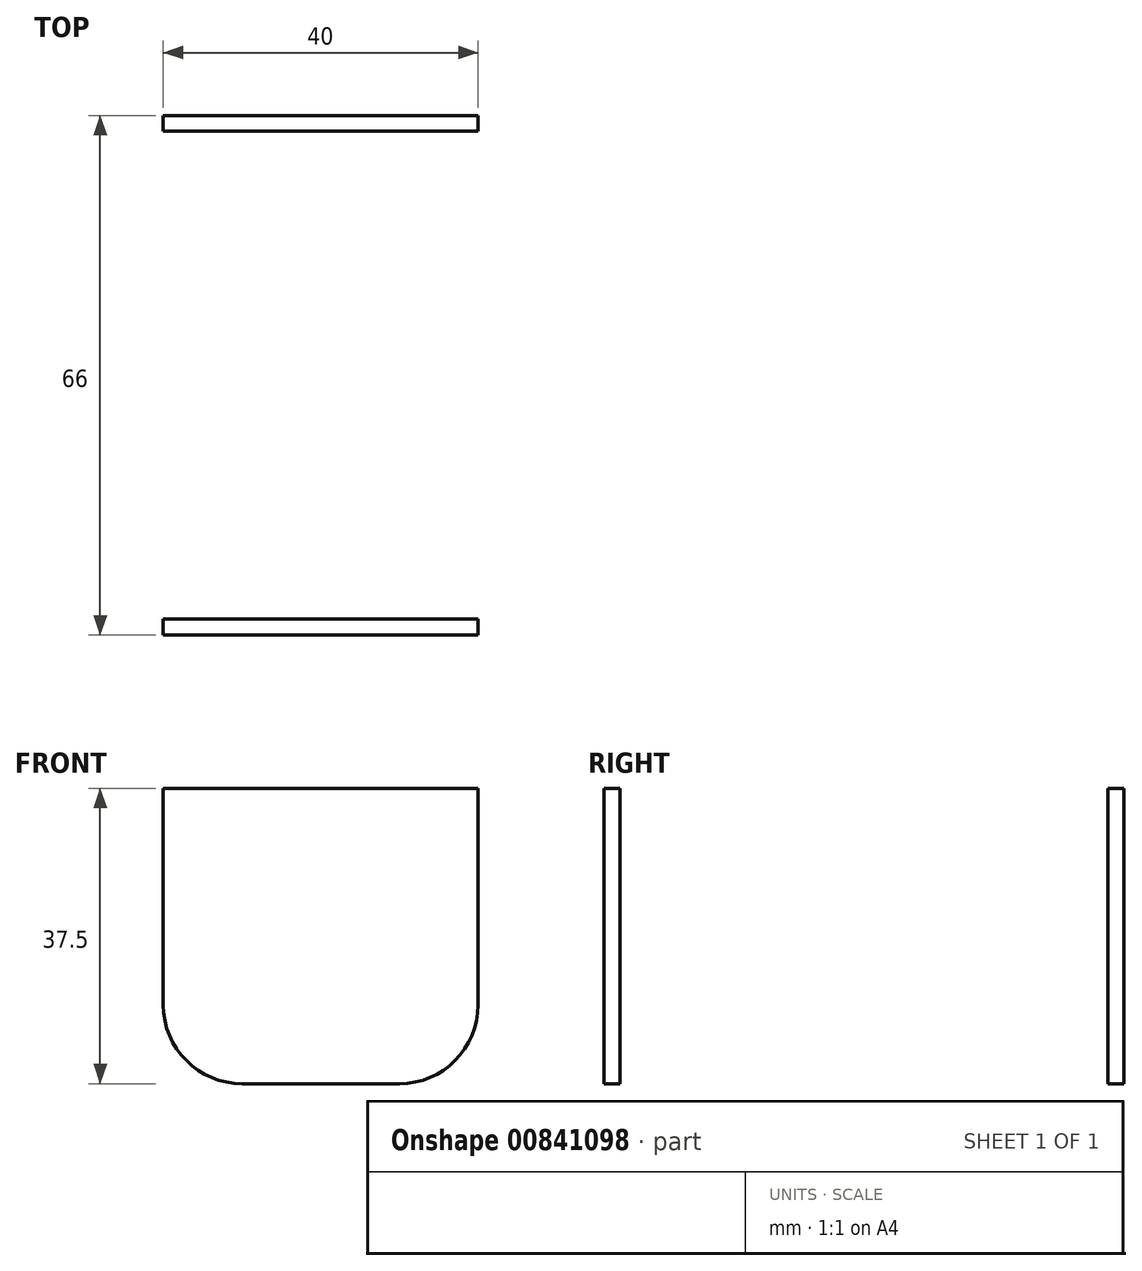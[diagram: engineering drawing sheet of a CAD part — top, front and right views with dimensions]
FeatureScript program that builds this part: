
annotation { "Feature Type Name" : "Feature", "Feature Type Description" : "" }
export const myFeature = defineFeature(function(context is Context, id is Id, definition is map)
    precondition{}
    {
        {
            var Q0;
            Q0=qCreatedBy(makeId("Top.planeOp"),FACE);
            var sketch = newSketch(context, id + "F0", { "sketchPlane" : qUnion([Q0])});
            skLineSegment(sketch, "E0.bottom", {"start": v(24.8, -33) * mm, "end": v(-24.8, -33) * mm});
            skLineSegment(sketch, "E0.top", {"start": v(24.8, 33) * mm, "end": v(-24.8, 33) * mm});
            skLineSegment(sketch, "E0.left", {"start": v(33, -24.8) * mm, "end": v(33, 24.8) * mm});
            skLineSegment(sketch, "E0.right", {"start": v(-33, -24.8) * mm, "end": v(-33, 24.8) * mm});
            skPoint(sketch, "E0.middle", {"position": v(0, 0) * mm});
            skPoint(sketch, "E1.visualSharp", {"position": v(-33, 33) * mm});
            skArc(sketch, "E1.filletArc", {"start": v(-24.8, 33) * mm, "mid": v(-30.6, 30.6) * mm, "end": v(-33, 24.8) * mm});
            skPoint(sketch, "E2.visualSharp", {"position": v(33, 33) * mm});
            skArc(sketch, "E2.filletArc", {"start": v(33, 24.8) * mm, "mid": v(30.6, 30.6) * mm, "end": v(24.8, 33) * mm});
            skPoint(sketch, "E3.visualSharp", {"position": v(33, -33) * mm});
            skArc(sketch, "E3.filletArc", {"start": v(24.8, -33) * mm, "mid": v(30.6, -30.6) * mm, "end": v(33, -24.8) * mm});
            skPoint(sketch, "E4.visualSharp", {"position": v(-33, -33) * mm});
            skArc(sketch, "E4.filletArc", {"start": v(-33, -24.8) * mm, "mid": v(-30.6, -30.6) * mm, "end": v(-24.8, -33) * mm});
            skSolve(sketch);
        }
        {
            var Q0;
            Q0=qSketchRegion(id+"F0",true);
            extrude(context, id + "F1", {"entities" : qUnion([Q0]), "oppositeDirection" : true, "depth" : 50 * mm, "offsetDistance" : 25 * mm});
        }
        {
            var Q0;
            Q0=makeQuery(id+"F1.opExtrude","CAP_EDGE",EDGE,{"disambiguationData":[OSD([sQuery(id+"F0.wireOp",EDGE,"E0.bottom")])],"isStart":false});
            fillet(context, id + "F2", {"entities" : qUnion([Q0]), "radius" : 5 * mm, "tangentPropagation" : true, "allowEdgeOverflow" : false});
        }
        {
            var Q0;
            Q0=makeQuery(id+"F1.opExtrude","CAP_FACE",FACE,{"disambiguationData":[OSD([sQuery(id+"F0.wireOp",EDGE,"E0.bottom"),sQuery(id+"F0.wireOp",EDGE,"E0.top"),sQuery(id+"F0.wireOp",EDGE,"E0.left"),sQuery(id+"F0.wireOp",EDGE,"E0.right"),sQuery(id+"F0.wireOp",EDGE,"E1.filletArc"),sQuery(id+"F0.wireOp",EDGE,"E2.filletArc"),sQuery(id+"F0.wireOp",EDGE,"E3.filletArc"),sQuery(id+"F0.wireOp",EDGE,"E4.filletArc")])],"isStart":false});
            var sketch = newSketch(context, id + "F3", { "sketchPlane" : qUnion([Q0])});
            skLineSegment(sketch, "E5.bottom", {"start": v(24.8, -28) * mm, "end": v(-24.8, -28) * mm});
            skLineSegment(sketch, "E5.top", {"start": v(24.8, 28) * mm, "end": v(-24.8, 28) * mm});
            skLineSegment(sketch, "E5.left", {"start": v(28, -24.8) * mm, "end": v(28, 24.8) * mm});
            skLineSegment(sketch, "E5.right", {"start": v(-28, -24.8) * mm, "end": v(-28, 24.8) * mm});
            skPoint(sketch, "E5.middle", {"position": v(0, 0) * mm});
            skPoint(sketch, "E6.visualSharp", {"position": v(28, 28) * mm});
            skArc(sketch, "E6.filletArc", {"start": v(28, 24.8) * mm, "mid": v(27.06, 27.06) * mm, "end": v(24.8, 28) * mm});
            skPoint(sketch, "E7.visualSharp", {"position": v(28, -28) * mm});
            skArc(sketch, "E7.filletArc", {"start": v(24.8, -28) * mm, "mid": v(27.06, -27.06) * mm, "end": v(28, -24.8) * mm});
            skPoint(sketch, "E8.visualSharp", {"position": v(-28, -28) * mm});
            skArc(sketch, "E8.filletArc", {"start": v(-28, -24.8) * mm, "mid": v(-27.06, -27.06) * mm, "end": v(-24.8, -28) * mm});
            skPoint(sketch, "E9.visualSharp", {"position": v(-28, 28) * mm});
            skArc(sketch, "E9.filletArc", {"start": v(-24.8, 28) * mm, "mid": v(-27.06, 27.06) * mm, "end": v(-28, 24.8) * mm});
            skArc(sketch, "E10.0", {"start": v(27, 24.8) * mm, "mid": v(26.36, 26.36) * mm, "end": v(24.8, 27) * mm});
            skLineSegment(sketch, "E10.1", {"start": v(27, -24.8) * mm, "end": v(27, 24.8) * mm});
            skLineSegment(sketch, "E10.2", {"start": v(24.8, 27) * mm, "end": v(-24.8, 27) * mm});
            skArc(sketch, "E10.3", {"start": v(24.8, -27) * mm, "mid": v(26.36, -26.36) * mm, "end": v(27, -24.8) * mm});
            skArc(sketch, "E10.4", {"start": v(-24.8, 27) * mm, "mid": v(-26.36, 26.36) * mm, "end": v(-27, 24.8) * mm});
            skLineSegment(sketch, "E10.5", {"start": v(-27, -24.8) * mm, "end": v(-27, 24.8) * mm});
            skArc(sketch, "E10.6", {"start": v(-27, -24.8) * mm, "mid": v(-26.36, -26.36) * mm, "end": v(-24.8, -27) * mm});
            skLineSegment(sketch, "E10.7", {"start": v(24.8, -27) * mm, "end": v(-24.8, -27) * mm});
            skSolve(sketch);
        }
        {
            var Q0;
            Q0=qSketchRegion(id+"F3",true);
            extrude(context, id + "F4", {"entities" : qUnion([Q0]), "operationType" : NewBodyOperationType.ADD, "depth" : 1 * mm, "offsetDistance" : 25 * mm});
        }
        {
            var Q0;
            Q0=makeQuery(id+"F1.opExtrude","CAP_FACE",FACE,{"disambiguationData":[OSD([sQuery(id+"F0.wireOp",EDGE,"E0.bottom"),sQuery(id+"F0.wireOp",EDGE,"E0.top"),sQuery(id+"F0.wireOp",EDGE,"E0.left"),sQuery(id+"F0.wireOp",EDGE,"E0.right"),sQuery(id+"F0.wireOp",EDGE,"E1.filletArc"),sQuery(id+"F0.wireOp",EDGE,"E2.filletArc"),sQuery(id+"F0.wireOp",EDGE,"E3.filletArc"),sQuery(id+"F0.wireOp",EDGE,"E4.filletArc")])],"isStart":true});
            shell(context, id + "F5", {"entities" : qUnion([Q0]), "thickness" : 2 * mm});
        }
        {
            var Q0;
            Q0=qCreatedBy(makeId("Top.planeOp"),FACE);
            cPlane(context, id + "F6", {"entities" : qUnion([Q0]), "cplaneType" : CPlaneType.OFFSET, "offset" : 3 * mm, "oppositeDirection" : true, "width" : 150 * mm, "height" : 150 * mm});
        }
        {
            var Q0;
            Q0=qCreatedBy(id+"F6.planeOp",FACE);
            var sketch = newSketch(context, id + "F7", { "sketchPlane" : qUnion([Q0])});
            skArc(sketch, "E11", {"start": v(24.8, -33) * mm, "mid": v(30.6, -30.6) * mm, "end": v(33, -24.8) * mm});
            skArc(sketch, "E12.0", {"start": v(24.8, -32) * mm, "mid": v(29.9, -29.9) * mm, "end": v(32, -24.8) * mm});
            skLineSegment(sketch, "E13", {"start": v(32, -24.8) * mm, "end": v(33, -24.8) * mm});
            skLineSegment(sketch, "E14", {"start": v(24.8, -32) * mm, "end": v(24.8, -33) * mm});
            skSolve(sketch);
        }
        {
            var Q0;
            Q0=qSketchRegion(id+"F7",true);
            extrude(context, id + "F8", {"entities" : qUnion([Q0]), "operationType" : NewBodyOperationType.REMOVE, "oppositeDirection" : true, "depth" : 1 * mm, "offsetDistance" : 25 * mm});
        }
        {
            var Q0;
            Q0=qCreatedBy(makeId("Front.planeOp"),FACE);
            var sketch = newSketch(context, id + "F9", { "sketchPlane" : qUnion([Q0])});
            skLineSegment(sketch, "E15", {"start": v(0, 0) * mm, "end": v(0, 11.9) * mm});
            skSolve(sketch);
        }
        {
            var Q0;
            Q0=makeQuery(id+"F1.opExtrude","SWEPT_BODY",BODY,{"disambiguationData":[OSD([sQuery(id+"F0.wireOp",EDGE,"E0.bottom"),sQuery(id+"F0.wireOp",EDGE,"E0.top"),sQuery(id+"F0.wireOp",EDGE,"E0.left"),sQuery(id+"F0.wireOp",EDGE,"E0.right"),sQuery(id+"F0.wireOp",EDGE,"E1.filletArc"),sQuery(id+"F0.wireOp",EDGE,"E2.filletArc"),sQuery(id+"F0.wireOp",EDGE,"E3.filletArc"),sQuery(id+"F0.wireOp",EDGE,"E4.filletArc")])]});
            var Q1;
            Q1=sQuery(id+"F9.wireOp",EDGE,"E15");
            circularPattern(context, id + "F10", {"entities" : qUnion([Q0]), "axis" : qUnion([Q1]), "angle" : 360 * degree, "instanceCount" : 4, "equalSpace" : true});
        }
        {
            var Q0;
            Q0=makeQuery(id+"F1.opExtrude","SWEPT_FACE",FACE,{"disambiguationData":[OSD([sQuery(id+"F0.wireOp",EDGE,"E0.bottom")])]});
            var sketch = newSketch(context, id + "F11", { "sketchPlane" : qUnion([Q0])});
            skLineSegment(sketch, "E16.bottom", {"start": v(10, -37.5) * mm, "end": v(-10, -37.5) * mm});
            skLineSegment(sketch, "E16.left", {"start": v(20, -27.5) * mm, "end": v(20, 0) * mm});
            skLineSegment(sketch, "E16.right", {"start": v(-20, -27.5) * mm, "end": v(-20, 0) * mm});
            skPoint(sketch, "E16.middle", {"position": v(0, 0) * mm});
            skPoint(sketch, "E17.visualSharp", {"position": v(-20, -37.5) * mm});
            skArc(sketch, "E17.filletArc", {"start": v(-20, -27.5) * mm, "mid": v(-17.07, -34.57) * mm, "end": v(-10, -37.5) * mm});
            skPoint(sketch, "E18.visualSharp", {"position": v(20, -37.5) * mm});
            skArc(sketch, "E18.filletArc", {"start": v(10, -37.5) * mm, "mid": v(17.07, -34.57) * mm, "end": v(20, -27.5) * mm});
            skLineSegment(sketch, "E19", {"start": v(0, 0) * mm, "end": v(20, 0) * mm});
            skLineSegment(sketch, "E20", {"start": v(20, 0) * mm, "end": v(-20, 0) * mm});
            skSolve(sketch);
        }
        {
            var Q0;
            Q0=qSketchRegion(id+"F11",true);
            extrude(context, id + "F12", {"entities" : qUnion([Q0]), "operationType" : NewBodyOperationType.INTERSECT, "endBound" : BoundingType.THROUGH_ALL, "oppositeDirection" : true, "depth" : 25 * mm, "offsetDistance" : 25 * mm});
        }
        {
            var Q0;
            Q0=makeQuery(id+"F12.boolean.opBoolean","SPLIT",BODY,{"disambiguationData":[OD(0.0)],"derivedFrom":makeQuery(id+"F10.opPattern","COPY",BODY,{"derivedFrom":makeQuery(id+"F1.opExtrude","SWEPT_BODY",BODY,{"disambiguationData":[OSD([sQuery(id+"F0.wireOp",EDGE,"E0.bottom"),sQuery(id+"F0.wireOp",EDGE,"E0.top"),sQuery(id+"F0.wireOp",EDGE,"E0.left"),sQuery(id+"F0.wireOp",EDGE,"E0.right"),sQuery(id+"F0.wireOp",EDGE,"E1.filletArc"),sQuery(id+"F0.wireOp",EDGE,"E2.filletArc"),sQuery(id+"F0.wireOp",EDGE,"E3.filletArc"),sQuery(id+"F0.wireOp",EDGE,"E4.filletArc")])]}),"instanceName":"1"})});
            var Q1;
            Q1=makeQuery(id+"F12.boolean.opBoolean","SPLIT",BODY,{"disambiguationData":[OD(1.0)],"derivedFrom":makeQuery(id+"F10.opPattern","COPY",BODY,{"derivedFrom":makeQuery(id+"F1.opExtrude","SWEPT_BODY",BODY,{"disambiguationData":[OSD([sQuery(id+"F0.wireOp",EDGE,"E0.bottom"),sQuery(id+"F0.wireOp",EDGE,"E0.top"),sQuery(id+"F0.wireOp",EDGE,"E0.left"),sQuery(id+"F0.wireOp",EDGE,"E0.right"),sQuery(id+"F0.wireOp",EDGE,"E1.filletArc"),sQuery(id+"F0.wireOp",EDGE,"E2.filletArc"),sQuery(id+"F0.wireOp",EDGE,"E3.filletArc"),sQuery(id+"F0.wireOp",EDGE,"E4.filletArc")])]}),"instanceName":"1"})});
            var Q2;
            Q2=makeQuery(id+"F12.boolean.opBoolean","SPLIT",BODY,{"disambiguationData":[OD(0.0)],"derivedFrom":makeQuery(id+"F10.opPattern","COPY",BODY,{"derivedFrom":makeQuery(id+"F1.opExtrude","SWEPT_BODY",BODY,{"disambiguationData":[OSD([sQuery(id+"F0.wireOp",EDGE,"E0.bottom"),sQuery(id+"F0.wireOp",EDGE,"E0.top"),sQuery(id+"F0.wireOp",EDGE,"E0.left"),sQuery(id+"F0.wireOp",EDGE,"E0.right"),sQuery(id+"F0.wireOp",EDGE,"E1.filletArc"),sQuery(id+"F0.wireOp",EDGE,"E2.filletArc"),sQuery(id+"F0.wireOp",EDGE,"E3.filletArc"),sQuery(id+"F0.wireOp",EDGE,"E4.filletArc")])]}),"instanceName":"2"})});
            var Q3;
            Q3=makeQuery(id+"F12.boolean.opBoolean","SPLIT",BODY,{"disambiguationData":[OD(1.0)],"derivedFrom":makeQuery(id+"F10.opPattern","COPY",BODY,{"derivedFrom":makeQuery(id+"F1.opExtrude","SWEPT_BODY",BODY,{"disambiguationData":[OSD([sQuery(id+"F0.wireOp",EDGE,"E0.bottom"),sQuery(id+"F0.wireOp",EDGE,"E0.top"),sQuery(id+"F0.wireOp",EDGE,"E0.left"),sQuery(id+"F0.wireOp",EDGE,"E0.right"),sQuery(id+"F0.wireOp",EDGE,"E1.filletArc"),sQuery(id+"F0.wireOp",EDGE,"E2.filletArc"),sQuery(id+"F0.wireOp",EDGE,"E3.filletArc"),sQuery(id+"F0.wireOp",EDGE,"E4.filletArc")])]}),"instanceName":"2"})});
            var Q4;
            Q4=makeQuery(id+"F12.boolean.opBoolean","SPLIT",BODY,{"disambiguationData":[OD(0.0)],"derivedFrom":makeQuery(id+"F10.opPattern","COPY",BODY,{"derivedFrom":makeQuery(id+"F1.opExtrude","SWEPT_BODY",BODY,{"disambiguationData":[OSD([sQuery(id+"F0.wireOp",EDGE,"E0.bottom"),sQuery(id+"F0.wireOp",EDGE,"E0.top"),sQuery(id+"F0.wireOp",EDGE,"E0.left"),sQuery(id+"F0.wireOp",EDGE,"E0.right"),sQuery(id+"F0.wireOp",EDGE,"E1.filletArc"),sQuery(id+"F0.wireOp",EDGE,"E2.filletArc"),sQuery(id+"F0.wireOp",EDGE,"E3.filletArc"),sQuery(id+"F0.wireOp",EDGE,"E4.filletArc")])]}),"instanceName":"3"})});
            var Q5;
            Q5=makeQuery(id+"F12.boolean.opBoolean","SPLIT",BODY,{"disambiguationData":[OD(1.0)],"derivedFrom":makeQuery(id+"F10.opPattern","COPY",BODY,{"derivedFrom":makeQuery(id+"F1.opExtrude","SWEPT_BODY",BODY,{"disambiguationData":[OSD([sQuery(id+"F0.wireOp",EDGE,"E0.bottom"),sQuery(id+"F0.wireOp",EDGE,"E0.top"),sQuery(id+"F0.wireOp",EDGE,"E0.left"),sQuery(id+"F0.wireOp",EDGE,"E0.right"),sQuery(id+"F0.wireOp",EDGE,"E1.filletArc"),sQuery(id+"F0.wireOp",EDGE,"E2.filletArc"),sQuery(id+"F0.wireOp",EDGE,"E3.filletArc"),sQuery(id+"F0.wireOp",EDGE,"E4.filletArc")])]}),"instanceName":"3"})});
            deleteBodies(context, id + "F13", {"entities" : qUnion([Q0, Q1, Q2, Q3, Q4, Q5])});
        }
    });
